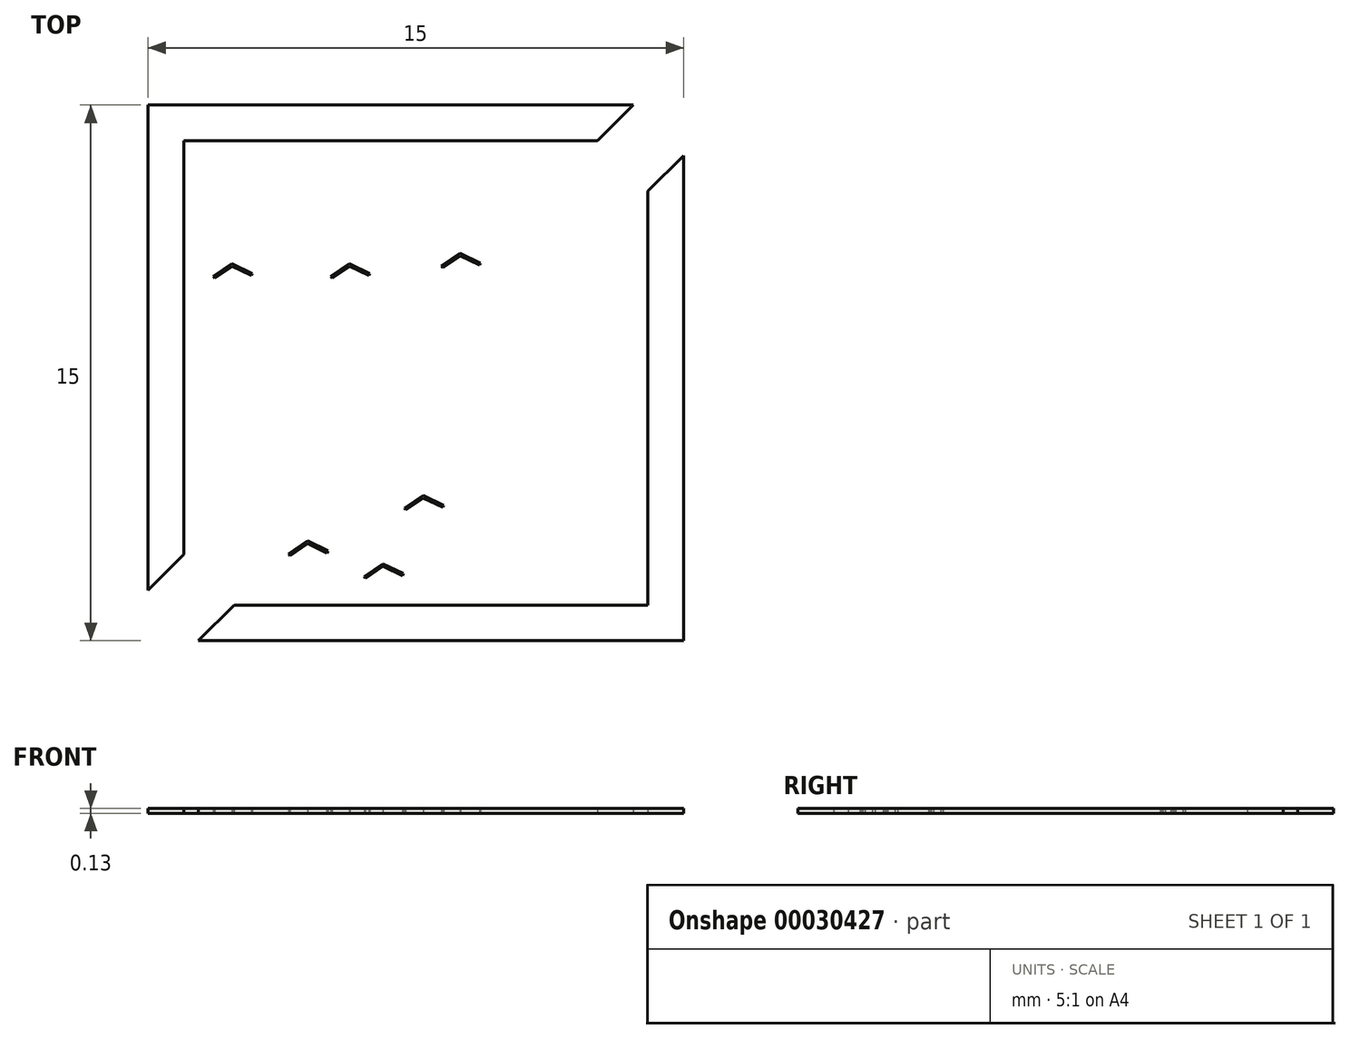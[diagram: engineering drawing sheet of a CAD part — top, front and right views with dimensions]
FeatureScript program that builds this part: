
annotation { "Feature Type Name" : "Feature", "Feature Type Description" : "" }
export const myFeature = defineFeature(function(context is Context, id is Id, definition is map)
    precondition{}
    {
        {
            var Q0;
            Q0=qCreatedBy(makeId("Top.planeOp"),FACE);
            var sketch = newSketch(context, id + "F0", { "sketchPlane" : qUnion([Q0])});
            skLineSegment(sketch, "E0.rect.bottom", {"start": v(6.09, 7.5) * mm, "end": v(-7.5, 7.5) * mm});
            skLineSegment(sketch, "E0.rect.top", {"start": v(7.5, -7.5) * mm, "end": v(-6.09, -7.5) * mm});
            skLineSegment(sketch, "E0.rect.left", {"start": v(7.5, 6.09) * mm, "end": v(7.5, -7.5) * mm});
            skLineSegment(sketch, "E0.rect.right", {"start": v(-7.5, 7.5) * mm, "end": v(-7.5, -6.09) * mm});
            skPoint(sketch, "E0.rect.middle", {"position": v(0, 0) * mm});
            skLineSegment(sketch, "E1.0", {"start": v(5.09, 6.5) * mm, "end": v(-6.5, 6.5) * mm});
            skLineSegment(sketch, "E2.0", {"start": v(-6.5, 6.5) * mm, "end": v(-6.5, -5.09) * mm});
            skLineSegment(sketch, "E3.0", {"start": v(6.5, 5.09) * mm, "end": v(6.5, -6.5) * mm});
            skLineSegment(sketch, "E4.0", {"start": v(6.5, -6.5) * mm, "end": v(-5.09, -6.5) * mm});
            skLineSegment(sketch, "E5.0", {"start": v(-5.64, 2.65) * mm, "end": v(-5.14, 2.98) * mm});
            skLineSegment(sketch, "E6.0", {"start": v(-5.14, 2.98) * mm, "end": v(-4.6, 2.72) * mm});
            skLineSegment(sketch, "E7", {"start": v(-5.67, 2.7) * mm, "end": v(-5.15, 3.06) * mm});
            skLineSegment(sketch, "E8", {"start": v(-5.15, 3.06) * mm, "end": v(-4.58, 2.78) * mm});
            skLineSegment(sketch, "E9", {"start": v(-4.58, 2.78) * mm, "end": v(-4.6, 2.72) * mm});
            skLineSegment(sketch, "E10", {"start": v(-5.67, 2.7) * mm, "end": v(-5.64, 2.65) * mm});
            skLineSegment(sketch, "E11.0", {"start": v(-2.34, 2.65) * mm, "end": v(-1.85, 2.98) * mm});
            skLineSegment(sketch, "E12.0", {"start": v(-1.85, 2.98) * mm, "end": v(-1.31, 2.72) * mm});
            skLineSegment(sketch, "E13", {"start": v(-2.38, 2.7) * mm, "end": v(-1.86, 3.06) * mm});
            skLineSegment(sketch, "E14", {"start": v(-1.86, 3.06) * mm, "end": v(-1.28, 2.78) * mm});
            skLineSegment(sketch, "E15", {"start": v(-1.28, 2.78) * mm, "end": v(-1.31, 2.72) * mm});
            skLineSegment(sketch, "E16", {"start": v(-2.38, 2.7) * mm, "end": v(-2.34, 2.65) * mm});
            skLineSegment(sketch, "E17.0", {"start": v(0.75, 2.94) * mm, "end": v(1.25, 3.28) * mm});
            skLineSegment(sketch, "E18.0", {"start": v(1.25, 3.28) * mm, "end": v(1.78, 3.02) * mm});
            skLineSegment(sketch, "E19", {"start": v(0.72, 3) * mm, "end": v(1.24, 3.35) * mm});
            skLineSegment(sketch, "E20", {"start": v(1.24, 3.35) * mm, "end": v(1.81, 3.08) * mm});
            skLineSegment(sketch, "E21", {"start": v(1.81, 3.08) * mm, "end": v(1.78, 3.02) * mm});
            skLineSegment(sketch, "E22", {"start": v(0.72, 3) * mm, "end": v(0.75, 2.94) * mm});
            skLineSegment(sketch, "E23.0", {"start": v(-3.52, -5.12) * mm, "end": v(-3.03, -4.78) * mm});
            skLineSegment(sketch, "E24.0", {"start": v(-3.03, -4.78) * mm, "end": v(-2.5, -5.04) * mm});
            skLineSegment(sketch, "E25", {"start": v(-3.56, -5.07) * mm, "end": v(-3.03, -4.7) * mm});
            skLineSegment(sketch, "E26", {"start": v(-3.03, -4.7) * mm, "end": v(-2.46, -4.98) * mm});
            skLineSegment(sketch, "E27", {"start": v(-2.46, -4.98) * mm, "end": v(-2.5, -5.04) * mm});
            skLineSegment(sketch, "E28", {"start": v(-3.56, -5.07) * mm, "end": v(-3.52, -5.12) * mm});
            skLineSegment(sketch, "E29.0", {"start": v(-1.41, -5.76) * mm, "end": v(-0.92, -5.42) * mm});
            skLineSegment(sketch, "E30.0", {"start": v(-0.92, -5.42) * mm, "end": v(-0.38, -5.68) * mm});
            skLineSegment(sketch, "E31", {"start": v(-1.45, -5.7) * mm, "end": v(-0.92, -5.35) * mm});
            skLineSegment(sketch, "E32", {"start": v(-0.92, -5.35) * mm, "end": v(-0.35, -5.62) * mm});
            skLineSegment(sketch, "E33", {"start": v(-0.35, -5.62) * mm, "end": v(-0.38, -5.68) * mm});
            skLineSegment(sketch, "E34", {"start": v(-1.45, -5.7) * mm, "end": v(-1.41, -5.76) * mm});
            skLineSegment(sketch, "E35.0", {"start": v(-0.28, -3.84) * mm, "end": v(0.21, -3.5) * mm});
            skLineSegment(sketch, "E36.0", {"start": v(0.21, -3.5) * mm, "end": v(0.75, -3.76) * mm});
            skLineSegment(sketch, "E37", {"start": v(-0.32, -3.79) * mm, "end": v(0.2, -3.43) * mm});
            skLineSegment(sketch, "E38", {"start": v(0.2, -3.43) * mm, "end": v(0.78, -3.7) * mm});
            skLineSegment(sketch, "E39", {"start": v(0.78, -3.7) * mm, "end": v(0.75, -3.76) * mm});
            skLineSegment(sketch, "E40", {"start": v(-0.32, -3.79) * mm, "end": v(-0.28, -3.84) * mm});
            skLineSegment(sketch, "E41.0", {"start": v(-6.5, -5.09) * mm, "end": v(-7.5, -6.09) * mm});
            skLineSegment(sketch, "E42.0", {"start": v(-5.09, -6.5) * mm, "end": v(-6.09, -7.5) * mm});
            skLineSegment(sketch, "E43.0", {"start": v(6.09, 7.5) * mm, "end": v(5.09, 6.5) * mm});
            skLineSegment(sketch, "E44.0", {"start": v(7.5, 6.09) * mm, "end": v(6.5, 5.09) * mm});
            skSolve(sketch);
        }
        {
            var Q0;
            Q0=makeQuery(id+"F0.imprint","IMPRINT",FACE,{"disambiguationData":[TD([[makeQuery(id+"F0.imprint","IMPRINT",EDGE,{"derivedFrom":sQuery(id+"F0.wireOp",EDGE,"E0.rect.bottom")}),1.0]])]});
            var Q1;
            Q1=makeQuery(id+"F0.imprint","IMPRINT",FACE,{"disambiguationData":[TD([[makeQuery(id+"F0.imprint","IMPRINT",EDGE,{"derivedFrom":sQuery(id+"F0.wireOp",EDGE,"E0.rect.top")}),-1.0]])]});
            extrude(context, id + "F1", {"entities" : qUnion([Q0, Q1]), "depth" : .13 * mm});
        }
        {
            var Q0;
            Q0 = qSketchRegion(id + "F0", true);
            extrude(context, id + "F2", {"entities" : qUnion([Q0]), "depth" : .13 * mm});
        }
    });
